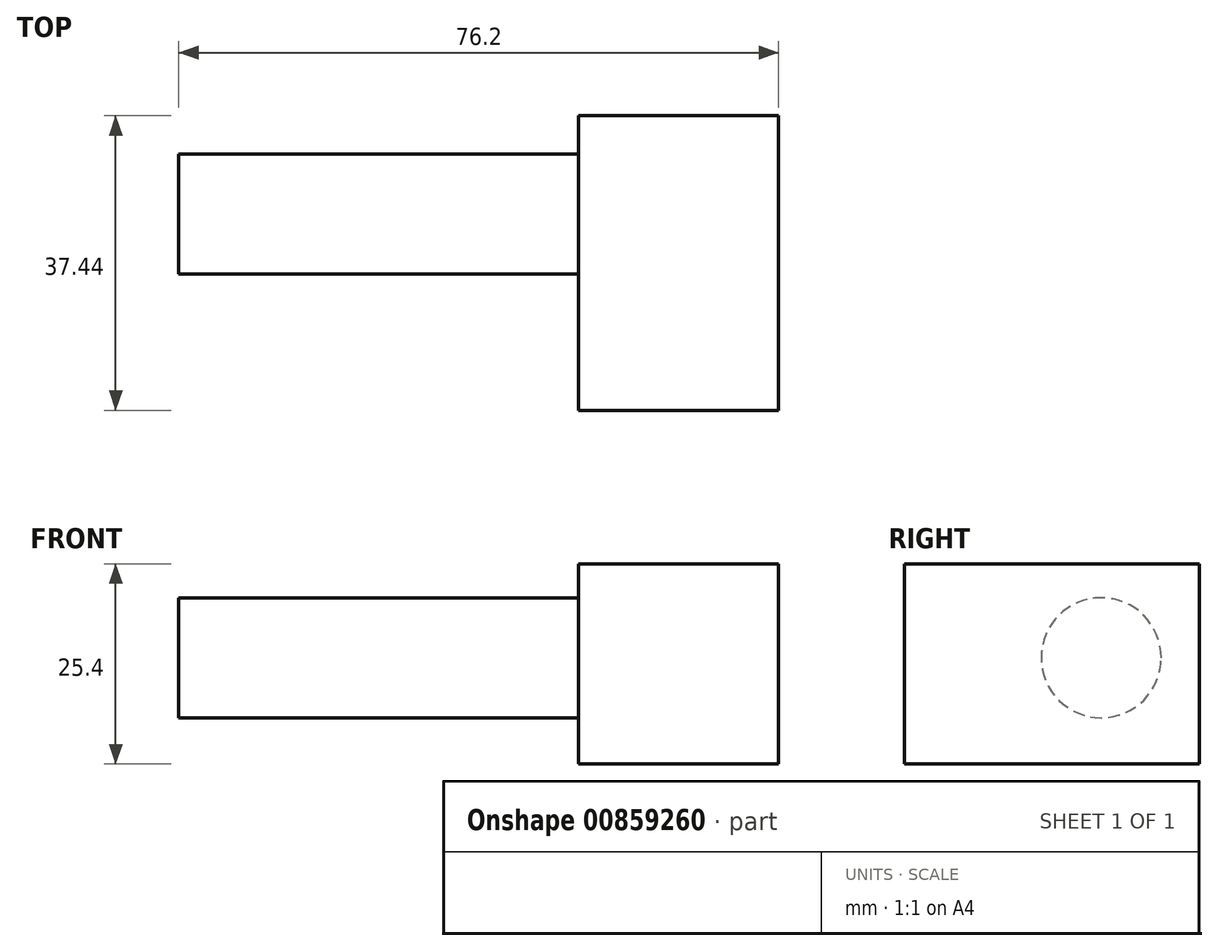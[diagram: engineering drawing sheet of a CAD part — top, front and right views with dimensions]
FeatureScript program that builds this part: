
annotation { "Feature Type Name" : "Feature", "Feature Type Description" : "" }
export const myFeature = defineFeature(function(context is Context, id is Id, definition is map)
    precondition{}
    {
        {
            var Q0;
            Q0=qCreatedBy(makeId("Top.planeOp"),FACE);
            var sketch = newSketch(context, id + "F0", { "sketchPlane" : qUnion([Q0])});
            skLineSegment(sketch, "E0.bottom", {"start": v(-25.4, 35.9) * mm, "end": v(0, 35.9) * mm});
            skLineSegment(sketch, "E0.top", {"start": v(-25.4, -1.53) * mm, "end": v(0, -1.53) * mm});
            skLineSegment(sketch, "E0.left", {"start": v(-25.4, 35.9) * mm, "end": v(-25.4, -1.53) * mm});
            skLineSegment(sketch, "E0.right", {"start": v(0, 35.9) * mm, "end": v(0, -1.53) * mm});
            skSolve(sketch);
        }
        {
            var Q0;
            Q0=makeQuery(id+"F0.imprint","IMPRINT",FACE,{"disambiguationData":[TD([[makeQuery(id+"F0.imprint","IMPRINT",EDGE,{"derivedFrom":sQuery(id+"F0.wireOp",EDGE,"E0.bottom")}),-1.0]])]});
            extrude(context, id + "F1", {"entities" : qUnion([Q0]), "depth" : 25.4 * mm, "offsetDistance" : 25.4 * mm});
        }
        {
            var Q0;
            Q0=makeQuery(id+"F1.opExtrude","SWEPT_FACE",FACE,{"disambiguationData":[OSD([sQuery(id+"F0.wireOp",EDGE,"E0.left")])]});
            var sketch = newSketch(context, id + "F2", { "sketchPlane" : qUnion([Q0])});
            skCircle(sketch, "E1", {"center": v(-23.44, 13.47) * mm, "radius": 7.62 * mm});
            skSolve(sketch);
        }
        {
            var Q0;
            Q0 = qSketchRegion(id + "F2", true);
            extrude(context, id + "F3", {"entities" : qUnion([Q0]), "operationType" : NewBodyOperationType.ADD, "depth" : 50.8 * mm, "offsetDistance" : 25.4 * mm});
        }
    });
